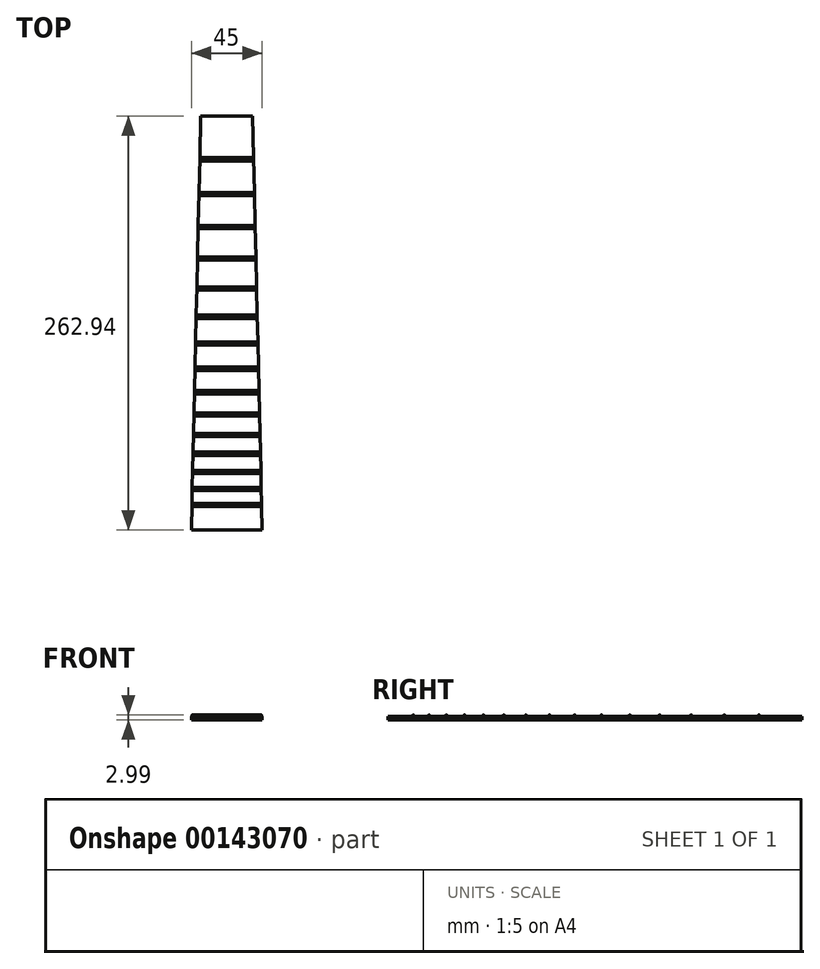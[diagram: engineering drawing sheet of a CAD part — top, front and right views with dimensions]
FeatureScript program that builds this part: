
annotation { "Feature Type Name" : "Feature", "Feature Type Description" : "" }
export const myFeature = defineFeature(function(context is Context, id is Id, definition is map)
    precondition{}
    {
        {
            var Q0;
            Q0=qCreatedBy(makeId("Top.planeOp"),FACE);
            var sketch = newSketch(context, id + "F0", { "sketchPlane" : qUnion([Q0])});
            skLineSegment(sketch, "E0", {"start": v(-15.06, 218.37) * mm, "end": v(17.94, 218.37) * mm});
            skLineSegment(sketch, "E1", {"start": v(17.94, 218.37) * mm, "end": v(23.94, -44.57) * mm});
            skLineSegment(sketch, "E2", {"start": v(23.94, -44.57) * mm, "end": v(-21.06, -44.57) * mm});
            skLineSegment(sketch, "E3", {"start": v(-21.06, -44.57) * mm, "end": v(-15.06, 218.37) * mm});
            skSolve(sketch);
        }
        {
            var Q0;
            Q0=makeQuery(id+"F0.imprint","IMPRINT",FACE,{"disambiguationData":[TD([[makeQuery(id+"F0.imprint","IMPRINT",EDGE,{"derivedFrom":sQuery(id+"F0.wireOp",EDGE,"E0")}),-1.0]])]});
            extrude(context, id + "F1", {"entities" : qUnion([Q0]), "depth" : 2 * mm});
        }
        {
            var Q0;
            Q0=makeQuery(id+"F1.opExtrude","CAP_FACE",FACE,{"disambiguationData":[OSD([sQuery(id+"F0.wireOp",EDGE,"E0"),sQuery(id+"F0.wireOp",EDGE,"E1"),sQuery(id+"F0.wireOp",EDGE,"E2"),sQuery(id+"F0.wireOp",EDGE,"E3")])],"isStart":false});
            var sketch = newSketch(context, id + "F2", { "sketchPlane" : qUnion([Q0])});
            skLineSegment(sketch, "E4.bottom", {"start": v(-20.67, -27.57) * mm, "end": v(23.6, -27.57) * mm});
            skLineSegment(sketch, "E4.top", {"start": v(-20.67, -29.57) * mm, "end": v(23.6, -29.57) * mm});
            skLineSegment(sketch, "E4.left", {"start": v(-20.67, -27.57) * mm, "end": v(-20.67, -29.57) * mm});
            skLineSegment(sketch, "E4.right", {"start": v(23.6, -27.57) * mm, "end": v(23.6, -29.57) * mm});
            skLineSegment(sketch, "E5.bottom", {"start": v(-20.44, -17.57) * mm, "end": v(23.32, -17.57) * mm});
            skLineSegment(sketch, "E5.top", {"start": v(-20.44, -19.57) * mm, "end": v(23.32, -19.57) * mm});
            skLineSegment(sketch, "E5.left", {"start": v(-20.44, -17.57) * mm, "end": v(-20.44, -19.57) * mm});
            skLineSegment(sketch, "E5.right", {"start": v(23.32, -17.57) * mm, "end": v(23.32, -19.57) * mm});
            skLineSegment(sketch, "E6.bottom", {"start": v(-20.2, -6.57) * mm, "end": v(23.07, -6.57) * mm});
            skLineSegment(sketch, "E6.top", {"start": v(-20.2, -8.57) * mm, "end": v(23.07, -8.57) * mm});
            skLineSegment(sketch, "E6.left", {"start": v(-20.2, -6.57) * mm, "end": v(-20.2, -8.57) * mm});
            skLineSegment(sketch, "E6.right", {"start": v(23.07, -6.57) * mm, "end": v(23.07, -8.57) * mm});
            skLineSegment(sketch, "E7.bottom", {"start": v(-19.93, 4.93) * mm, "end": v(22.81, 4.93) * mm});
            skLineSegment(sketch, "E7.top", {"start": v(-19.93, 2.93) * mm, "end": v(22.81, 2.93) * mm});
            skLineSegment(sketch, "E7.left", {"start": v(-19.93, 4.93) * mm, "end": v(-19.93, 2.93) * mm});
            skLineSegment(sketch, "E7.right", {"start": v(22.81, 4.93) * mm, "end": v(22.81, 2.93) * mm});
            skLineSegment(sketch, "E8.bottom", {"start": v(-19.66, 16.93) * mm, "end": v(22.54, 16.93) * mm});
            skLineSegment(sketch, "E8.top", {"start": v(-19.66, 14.93) * mm, "end": v(22.54, 14.93) * mm});
            skLineSegment(sketch, "E8.left", {"start": v(-19.66, 16.93) * mm, "end": v(-19.66, 14.93) * mm});
            skLineSegment(sketch, "E8.right", {"start": v(22.54, 16.93) * mm, "end": v(22.54, 14.93) * mm});
            skLineSegment(sketch, "E9.bottom", {"start": v(-19.36, 29.93) * mm, "end": v(22.24, 29.93) * mm});
            skLineSegment(sketch, "E9.top", {"start": v(-19.36, 27.93) * mm, "end": v(22.24, 27.93) * mm});
            skLineSegment(sketch, "E9.left", {"start": v(-19.36, 29.93) * mm, "end": v(-19.36, 27.93) * mm});
            skLineSegment(sketch, "E9.right", {"start": v(22.24, 29.93) * mm, "end": v(22.24, 27.93) * mm});
            skLineSegment(sketch, "E10.bottom", {"start": v(-19.04, 43.93) * mm, "end": v(21.92, 43.93) * mm});
            skLineSegment(sketch, "E10.top", {"start": v(-19.04, 41.93) * mm, "end": v(21.92, 41.93) * mm});
            skLineSegment(sketch, "E10.left", {"start": v(-19.04, 43.93) * mm, "end": v(-19.04, 41.93) * mm});
            skLineSegment(sketch, "E10.right", {"start": v(21.92, 43.93) * mm, "end": v(21.92, 41.93) * mm});
            skLineSegment(sketch, "E11.bottom", {"start": v(-18.7, 58.93) * mm, "end": v(21.58, 58.93) * mm});
            skLineSegment(sketch, "E11.top", {"start": v(-18.7, 56.93) * mm, "end": v(21.58, 56.93) * mm});
            skLineSegment(sketch, "E11.left", {"start": v(-18.7, 58.93) * mm, "end": v(-18.7, 56.93) * mm});
            skLineSegment(sketch, "E11.right", {"start": v(21.58, 58.93) * mm, "end": v(21.58, 56.93) * mm});
            skLineSegment(sketch, "E12.bottom", {"start": v(-18.33, 74.93) * mm, "end": v(21.21, 74.93) * mm});
            skLineSegment(sketch, "E12.top", {"start": v(-18.33, 72.93) * mm, "end": v(21.21, 72.93) * mm});
            skLineSegment(sketch, "E12.left", {"start": v(-18.33, 74.93) * mm, "end": v(-18.33, 72.93) * mm});
            skLineSegment(sketch, "E12.right", {"start": v(21.21, 74.93) * mm, "end": v(21.21, 72.93) * mm});
            skLineSegment(sketch, "E13.bottom", {"start": v(-17.94, 91.93) * mm, "end": v(20.83, 91.93) * mm});
            skLineSegment(sketch, "E13.top", {"start": v(-17.94, 89.93) * mm, "end": v(20.83, 89.93) * mm});
            skLineSegment(sketch, "E13.left", {"start": v(-17.94, 91.93) * mm, "end": v(-17.94, 89.93) * mm});
            skLineSegment(sketch, "E13.right", {"start": v(20.83, 91.93) * mm, "end": v(20.83, 89.93) * mm});
            skLineSegment(sketch, "E14.bottom", {"start": v(-17.53, 109.93) * mm, "end": v(20.41, 109.93) * mm});
            skLineSegment(sketch, "E14.top", {"start": v(-17.53, 107.93) * mm, "end": v(20.41, 107.93) * mm});
            skLineSegment(sketch, "E14.left", {"start": v(-17.53, 109.93) * mm, "end": v(-17.53, 107.93) * mm});
            skLineSegment(sketch, "E14.right", {"start": v(20.41, 109.93) * mm, "end": v(20.41, 107.93) * mm});
            skLineSegment(sketch, "E15.bottom", {"start": v(-17.1, 128.93) * mm, "end": v(19.98, 128.93) * mm});
            skLineSegment(sketch, "E15.top", {"start": v(-17.1, 126.93) * mm, "end": v(19.98, 126.93) * mm});
            skLineSegment(sketch, "E15.left", {"start": v(-17.1, 128.93) * mm, "end": v(-17.1, 126.93) * mm});
            skLineSegment(sketch, "E15.right", {"start": v(19.98, 128.93) * mm, "end": v(19.98, 126.93) * mm});
            skLineSegment(sketch, "E16.bottom", {"start": v(-16.64, 148.93) * mm, "end": v(19.52, 148.93) * mm});
            skLineSegment(sketch, "E16.top", {"start": v(-16.64, 146.93) * mm, "end": v(19.52, 146.93) * mm});
            skLineSegment(sketch, "E16.left", {"start": v(-16.64, 148.93) * mm, "end": v(-16.64, 146.93) * mm});
            skLineSegment(sketch, "E16.right", {"start": v(19.52, 148.93) * mm, "end": v(19.52, 146.93) * mm});
            skLineSegment(sketch, "E17.bottom", {"start": v(-16.16, 169.93) * mm, "end": v(19.05, 169.93) * mm});
            skLineSegment(sketch, "E17.top", {"start": v(-16.16, 167.93) * mm, "end": v(19.05, 167.93) * mm});
            skLineSegment(sketch, "E17.left", {"start": v(-16.16, 169.93) * mm, "end": v(-16.16, 167.93) * mm});
            skLineSegment(sketch, "E17.right", {"start": v(19.05, 169.93) * mm, "end": v(19.05, 167.93) * mm});
            skLineSegment(sketch, "E18.bottom", {"start": v(-15.66, 191.93) * mm, "end": v(18.54, 191.93) * mm});
            skLineSegment(sketch, "E18.top", {"start": v(-15.66, 189.93) * mm, "end": v(18.54, 189.93) * mm});
            skLineSegment(sketch, "E18.left", {"start": v(-15.66, 191.93) * mm, "end": v(-15.66, 189.93) * mm});
            skLineSegment(sketch, "E18.right", {"start": v(18.54, 191.93) * mm, "end": v(18.54, 189.93) * mm});
            skSolve(sketch);
        }
        {
            var Q0;
            Q0 = qSketchRegion(id + "F2", true);
            extrude(context, id + "F3", {"entities" : qUnion([Q0]), "operationType" : NewBodyOperationType.ADD, "depth" : 1 * mm});
        }
        {
            var Q0;
            Q0=makeQuery(id+"F3.opExtrude","CAP_EDGE",EDGE,{"disambiguationData":[OSD([sQuery(id+"F2.wireOp",EDGE,"E4.top")])],"isStart":false});
            var Q1;
            Q1=makeQuery(id+"F3.opExtrude","CAP_EDGE",EDGE,{"disambiguationData":[OSD([sQuery(id+"F2.wireOp",EDGE,"E4.bottom")])],"isStart":false});
            var Q2;
            Q2=makeQuery(id+"F3.opExtrude","CAP_EDGE",EDGE,{"disambiguationData":[OSD([sQuery(id+"F2.wireOp",EDGE,"E5.top")])],"isStart":false});
            var Q3;
            Q3=makeQuery(id+"F3.opExtrude","CAP_EDGE",EDGE,{"disambiguationData":[OSD([sQuery(id+"F2.wireOp",EDGE,"E5.bottom")])],"isStart":false});
            var Q4;
            Q4=makeQuery(id+"F3.opExtrude","CAP_EDGE",EDGE,{"disambiguationData":[OSD([sQuery(id+"F2.wireOp",EDGE,"E6.top")])],"isStart":false});
            var Q5;
            Q5=makeQuery(id+"F3.opExtrude","CAP_EDGE",EDGE,{"disambiguationData":[OSD([sQuery(id+"F2.wireOp",EDGE,"E6.bottom")])],"isStart":false});
            var Q6;
            Q6=makeQuery(id+"F3.opExtrude","CAP_EDGE",EDGE,{"disambiguationData":[OSD([sQuery(id+"F2.wireOp",EDGE,"E7.top")])],"isStart":false});
            var Q7;
            Q7=makeQuery(id+"F3.opExtrude","CAP_EDGE",EDGE,{"disambiguationData":[OSD([sQuery(id+"F2.wireOp",EDGE,"E7.bottom")])],"isStart":false});
            var Q8;
            Q8=makeQuery(id+"F3.opExtrude","CAP_EDGE",EDGE,{"disambiguationData":[OSD([sQuery(id+"F2.wireOp",EDGE,"E8.top")])],"isStart":false});
            var Q9;
            Q9=makeQuery(id+"F3.opExtrude","CAP_EDGE",EDGE,{"disambiguationData":[OSD([sQuery(id+"F2.wireOp",EDGE,"E8.bottom")])],"isStart":false});
            var Q10;
            Q10=makeQuery(id+"F3.opExtrude","CAP_EDGE",EDGE,{"disambiguationData":[OSD([sQuery(id+"F2.wireOp",EDGE,"E9.top")])],"isStart":false});
            var Q11;
            Q11=makeQuery(id+"F3.opExtrude","CAP_EDGE",EDGE,{"disambiguationData":[OSD([sQuery(id+"F2.wireOp",EDGE,"E9.bottom")])],"isStart":false});
            var Q12;
            Q12=makeQuery(id+"F3.opExtrude","CAP_EDGE",EDGE,{"disambiguationData":[OSD([sQuery(id+"F2.wireOp",EDGE,"E10.top")])],"isStart":false});
            var Q13;
            Q13=makeQuery(id+"F3.opExtrude","CAP_EDGE",EDGE,{"disambiguationData":[OSD([sQuery(id+"F2.wireOp",EDGE,"E10.bottom")])],"isStart":false});
            var Q14;
            Q14=makeQuery(id+"F3.opExtrude","CAP_EDGE",EDGE,{"disambiguationData":[OSD([sQuery(id+"F2.wireOp",EDGE,"E11.top")])],"isStart":false});
            var Q15;
            Q15=makeQuery(id+"F3.opExtrude","CAP_EDGE",EDGE,{"disambiguationData":[OSD([sQuery(id+"F2.wireOp",EDGE,"E11.bottom")])],"isStart":false});
            var Q16;
            Q16=makeQuery(id+"F3.opExtrude","CAP_EDGE",EDGE,{"disambiguationData":[OSD([sQuery(id+"F2.wireOp",EDGE,"E12.top")])],"isStart":false});
            var Q17;
            Q17=makeQuery(id+"F3.opExtrude","CAP_EDGE",EDGE,{"disambiguationData":[OSD([sQuery(id+"F2.wireOp",EDGE,"E12.bottom")])],"isStart":false});
            var Q18;
            Q18=makeQuery(id+"F3.opExtrude","CAP_EDGE",EDGE,{"disambiguationData":[OSD([sQuery(id+"F2.wireOp",EDGE,"E13.top")])],"isStart":false});
            var Q19;
            Q19=makeQuery(id+"F3.opExtrude","CAP_EDGE",EDGE,{"disambiguationData":[OSD([sQuery(id+"F2.wireOp",EDGE,"E13.bottom")])],"isStart":false});
            var Q20;
            Q20=makeQuery(id+"F3.opExtrude","CAP_EDGE",EDGE,{"disambiguationData":[OSD([sQuery(id+"F2.wireOp",EDGE,"E14.top")])],"isStart":false});
            var Q21;
            Q21=makeQuery(id+"F3.opExtrude","CAP_EDGE",EDGE,{"disambiguationData":[OSD([sQuery(id+"F2.wireOp",EDGE,"E14.bottom")])],"isStart":false});
            var Q22;
            Q22=makeQuery(id+"F3.opExtrude","CAP_EDGE",EDGE,{"disambiguationData":[OSD([sQuery(id+"F2.wireOp",EDGE,"E15.top")])],"isStart":false});
            var Q23;
            Q23=makeQuery(id+"F3.opExtrude","CAP_EDGE",EDGE,{"disambiguationData":[OSD([sQuery(id+"F2.wireOp",EDGE,"E15.bottom")])],"isStart":false});
            var Q24;
            Q24=makeQuery(id+"F3.opExtrude","CAP_EDGE",EDGE,{"disambiguationData":[OSD([sQuery(id+"F2.wireOp",EDGE,"E16.top")])],"isStart":false});
            var Q25;
            Q25=makeQuery(id+"F3.opExtrude","CAP_EDGE",EDGE,{"disambiguationData":[OSD([sQuery(id+"F2.wireOp",EDGE,"E16.bottom")])],"isStart":false});
            var Q26;
            Q26=makeQuery(id+"F3.opExtrude","CAP_EDGE",EDGE,{"disambiguationData":[OSD([sQuery(id+"F2.wireOp",EDGE,"E17.top")])],"isStart":false});
            var Q27;
            Q27=makeQuery(id+"F3.opExtrude","CAP_EDGE",EDGE,{"disambiguationData":[OSD([sQuery(id+"F2.wireOp",EDGE,"E17.bottom")])],"isStart":false});
            var Q28;
            Q28=makeQuery(id+"F3.opExtrude","CAP_EDGE",EDGE,{"disambiguationData":[OSD([sQuery(id+"F2.wireOp",EDGE,"E18.top")])],"isStart":false});
            var Q29;
            Q29=makeQuery(id+"F3.opExtrude","CAP_EDGE",EDGE,{"disambiguationData":[OSD([sQuery(id+"F2.wireOp",EDGE,"E18.bottom")])],"isStart":false});
            fillet(context, id + "F4", {"entities" : qUnion([Q0, Q1, Q2, Q3, Q4, Q5, Q6, Q7, Q8, Q9, Q10, Q11, Q12, Q13, Q14, Q15, Q16, Q17, Q18, Q19, Q20, Q21, Q22, Q23, Q24, Q25, Q26, Q27, Q28, Q29]), "radius" : 1.2 * mm, "tangentPropagation" : true, "allowEdgeOverflow" : false});
        }
    });
